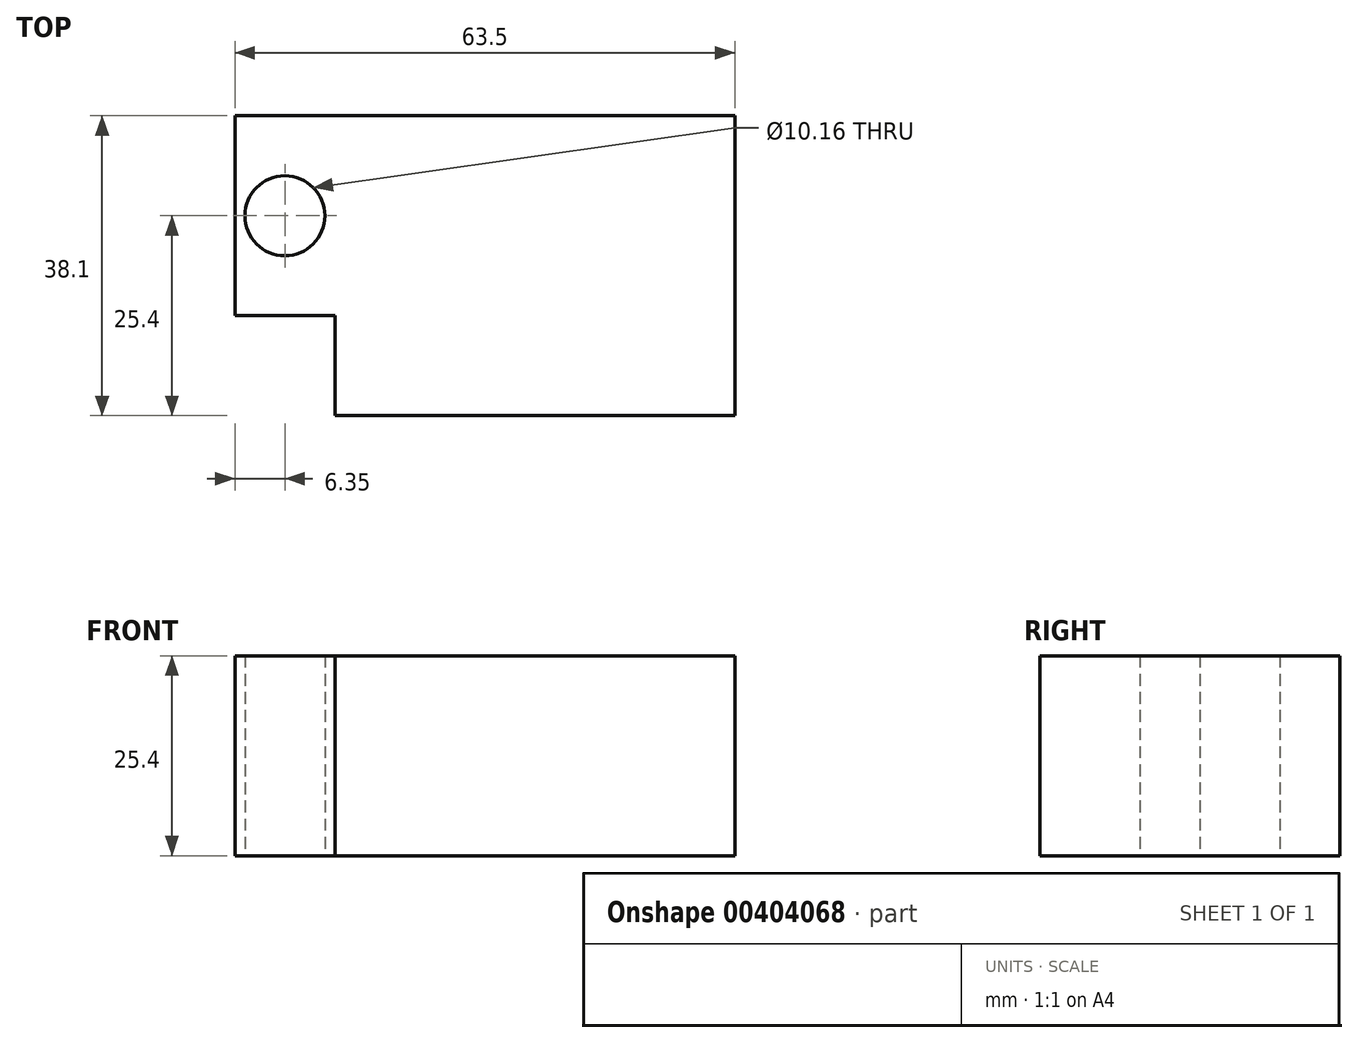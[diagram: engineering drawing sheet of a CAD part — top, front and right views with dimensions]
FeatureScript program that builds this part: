
annotation { "Feature Type Name" : "Feature", "Feature Type Description" : "" }
export const myFeature = defineFeature(function(context is Context, id is Id, definition is map)
    precondition{}
    {
        {
            var Q0;
            Q0=qCreatedBy(makeId("Top.planeOp"),FACE);
            var sketch = newSketch(context, id + "F0", { "sketchPlane" : qUnion([Q0])});
            skLineSegment(sketch, "E0.bottom", {"start": v(25.4, -6.35) * mm, "end": v(-25.4, -6.35) * mm});
            skLineSegment(sketch, "E0.top", {"start": v(25.4, 6.35) * mm, "end": v(-25.4, 6.35) * mm});
            skLineSegment(sketch, "E0.left", {"start": v(25.4, -6.35) * mm, "end": v(25.4, 6.35) * mm});
            skLineSegment(sketch, "E0.right", {"start": v(-25.4, -6.35) * mm, "end": v(-25.4, 6.35) * mm});
            skPoint(sketch, "E0.middle", {"position": v(0, 0) * mm});
            skLineSegment(sketch, "E1", {"start": v(25.4, 6.35) * mm, "end": v(25.4, 31.75) * mm});
            skLineSegment(sketch, "E2", {"start": v(25.4, 31.75) * mm, "end": v(-25.4, 31.75) * mm});
            skLineSegment(sketch, "E3", {"start": v(-25.4, 31.75) * mm, "end": v(-25.4, 6.35) * mm});
            skLineSegment(sketch, "E4", {"start": v(-25.4, 31.75) * mm, "end": v(-38.1, 31.75) * mm});
            skLineSegment(sketch, "E5", {"start": v(-38.1, 31.75) * mm, "end": v(-38.1, 6.35) * mm});
            skLineSegment(sketch, "E6", {"start": v(-38.1, 6.35) * mm, "end": v(-25.4, 6.35) * mm});
            skLineSegment(sketch, "E7", {"start": v(-25.4, 19.05) * mm, "end": v(-38.1, 19.05) * mm});
            skLineSegment(sketch, "E8", {"start": v(-31.75, 31.75) * mm, "end": v(-31.75, 6.35) * mm});
            skPoint(sketch, "E9", {"position": v(-31.75, 19.05) * mm});
            skCircle(sketch, "E10", {"center": v(-31.75, 19.05) * mm, "radius": 5.08 * mm});
            skSolve(sketch);
        }
        {
            var Q0;
            Q0=makeQuery(id+"F0.imprint","IMPRINT",FACE,{"disambiguationData":[TD([[makeQuery(id+"F0.imprint","IMPRINT",EDGE,{"derivedFrom":sQuery(id+"F0.wireOp",EDGE,"E0.bottom")}),-1.0]])]});
            extrude(context, id + "F1", {"entities" : qUnion([Q0]), "endBound" : BoundingType.SYMMETRIC, "depth" : 25.4 * mm});
        }
        {
            var Q0;
            {var subQ3=sQuery(id+"F0.wireOp",EDGE,"E0.top");Q0=makeQuery(id+"F0.imprint","IMPRINT",FACE,{"disambiguationData":[TD([[makeQuery(id+"F0.imprint","IMPRINT",EDGE,{"derivedFrom":subQ3}),-1.0]])]});}
            var Q1;
            {var subQ0=sQuery(id+"F0.wireOp",EDGE,"E7");var subQ1=sQuery(id+"F0.wireOp",EDGE,"E3");var subQ2=makeQuery(id+"F0.imprint","INTERSECT",VERTEX,{"derivedFrom":[subQ1,subQ0]});Q1=makeQuery(id+"F0.imprint","IMPRINT",FACE,{"disambiguationData":[TD([[makeQuery(id+"F0.imprint","IMPRINT",EDGE,{"disambiguationData":[TD([[subQ2,-1.0]])],"derivedFrom":subQ0}),-1.0]])]});}
            var Q2;
            {var subQ1=sQuery(id+"F0.wireOp",EDGE,"E4");var subQ6=sQuery(id+"F0.wireOp",EDGE,"E5");var subQ9=makeQuery(id+"F0.imprint","INTERSECT",VERTEX,{"derivedFrom":[subQ1,subQ6]});Q2=makeQuery(id+"F0.imprint","IMPRINT",FACE,{"disambiguationData":[TD([[makeQuery(id+"F0.imprint","IMPRINT",EDGE,{"disambiguationData":[TD([[subQ9,1.0]])],"derivedFrom":subQ1}),1.0]])]});}
            var Q3;
            {var subQ1=sQuery(id+"F0.wireOp",EDGE,"E5");var subQ5=sQuery(id+"F0.wireOp",EDGE,"E6");var subQ6=makeQuery(id+"F0.imprint","INTERSECT",VERTEX,{"derivedFrom":[subQ1,subQ5]});Q3=makeQuery(id+"F0.imprint","IMPRINT",FACE,{"disambiguationData":[TD([[makeQuery(id+"F0.imprint","IMPRINT",EDGE,{"disambiguationData":[TD([[subQ6,1.0]])],"derivedFrom":subQ1}),1.0]])]});}
            var Q4;
            {var subQ5=sQuery(id+"F0.wireOp",EDGE,"E7");var subQ6=sQuery(id+"F0.wireOp",EDGE,"E3");var subQ7=makeQuery(id+"F0.imprint","INTERSECT",VERTEX,{"derivedFrom":[subQ6,subQ5]});Q4=makeQuery(id+"F0.imprint","IMPRINT",FACE,{"disambiguationData":[TD([[makeQuery(id+"F0.imprint","IMPRINT",EDGE,{"disambiguationData":[TD([[subQ7,-1.0]])],"derivedFrom":subQ5}),1.0]])]});}
            extrude(context, id + "F2", {"entities" : qUnion([Q0, Q1, Q2, Q3, Q4]), "operationType" : NewBodyOperationType.ADD, "endBound" : BoundingType.SYMMETRIC, "depth" : 25.4 * mm});
        }
    });
